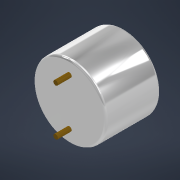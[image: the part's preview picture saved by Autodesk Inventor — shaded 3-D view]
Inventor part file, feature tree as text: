
AUTODESK INVENTOR PART (.ipt)
format: ipt  version: 2021 (Build 250183000, 183)  size: 165,376 bytes
history: native  units: mm
features: extrude x1, sketch x1, projected_geometry x1, imported_body x1
ambient origin geometry x8: Origin, YZ Plane, XZ Plane, XY Plane, X Axis, Y Axis, Z Axis, Center Point
bodies: Solid1 (feature_tree)
feature tree (4):
  extrude  "Pins"  Depth=1.0mm
  sketch  "Sketch1"  dims[d0=1.0mm d1=1.0mm d2=10.2mm d3=3.0mm d4=0.0mm]
  projected_geometry  "Projected Loop1"
  imported_body  "Base1"
